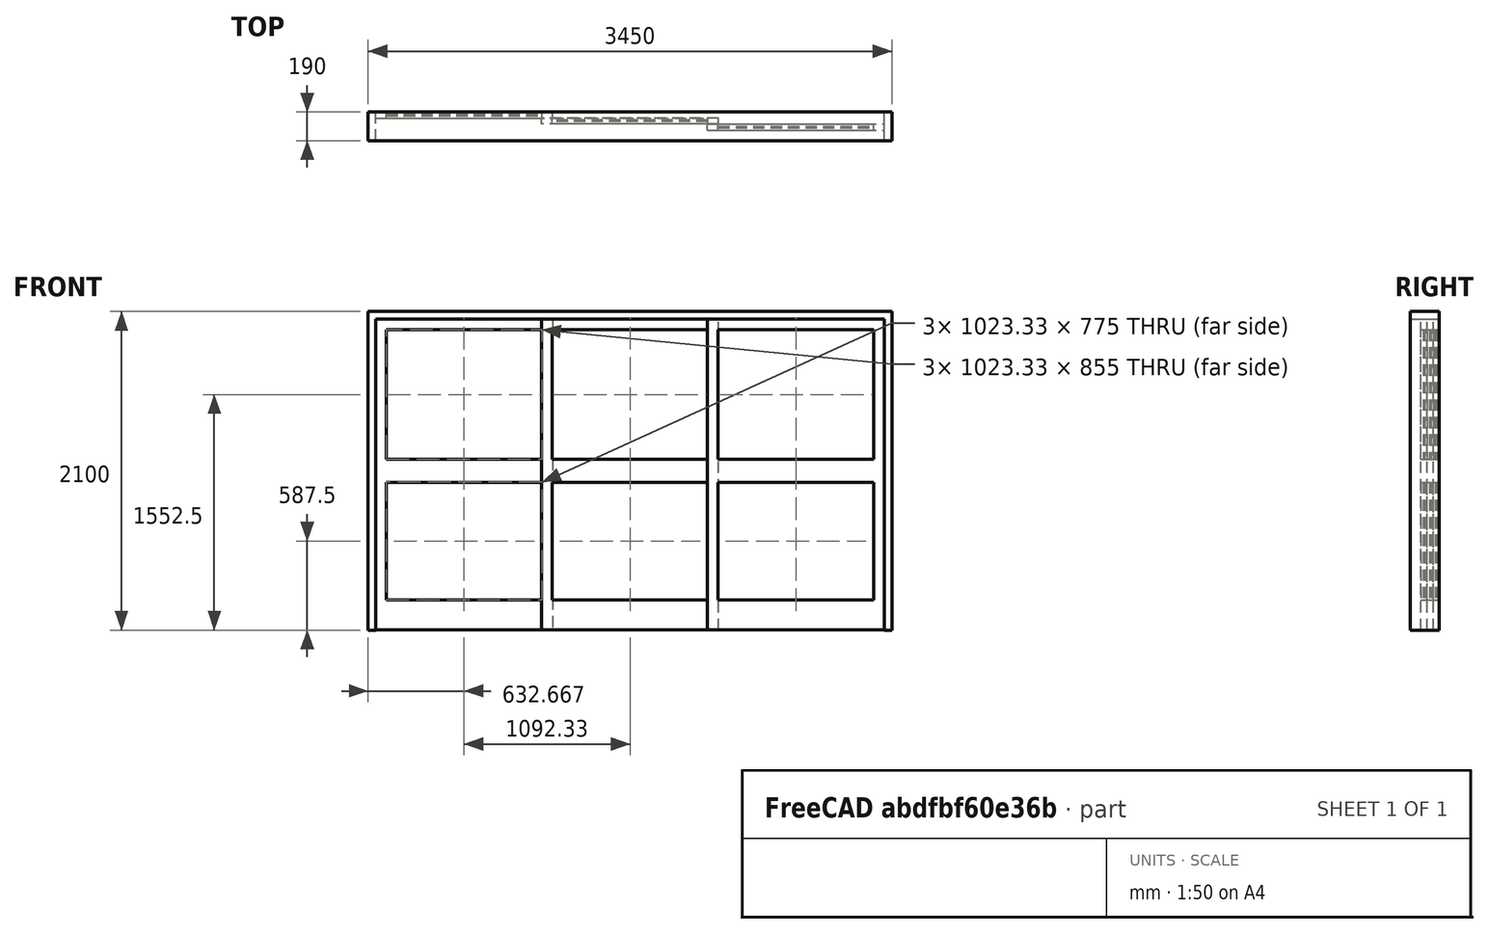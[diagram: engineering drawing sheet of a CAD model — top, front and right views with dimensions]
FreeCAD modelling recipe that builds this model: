
FCSTD DOCUMENT  (FreeCAD 0.16R6704 (Git))
Label: Slinding door 3 sheets with glass
License: CreativeCommons Attribution
LicenseURL: http://creativecommons.org/licenses/by/4.0/
objects: Sketcher::SketchObject×1, Part::FeaturePython×1
note: 2 computed .brp shape members not serialized (recipe doc carries the construction recipe); baked Part::Feature solids carry a one-line shape summary decoded from their .brp

FEATURE [Sketcher::SketchObject] Sketch182  label="Sketch"
  Placement = pos=(0,0,0) rot=(1,0,0;1.5708rad)
  sketch-geometry (45):
    g0: LineSegment StartX=0 StartY=0 StartZ=0 EndX=3450 EndY=0 EndZ=0
    g1: LineSegment StartX=3450 StartY=0 StartZ=0 EndX=3450 EndY=2100 EndZ=0
    g2: LineSegment StartX=3450 StartY=2100 StartZ=0 EndX=0 EndY=2100 EndZ=0
    g3: LineSegment StartX=0 StartY=2100 StartZ=0 EndX=0 EndY=0 EndZ=0
    g4: LineSegment StartX=50 StartY=0 StartZ=0 EndX=3400 EndY=0 EndZ=0
    g5: LineSegment StartX=3400 StartY=0 StartZ=0 EndX=3400 EndY=2050 EndZ=0
    g6: LineSegment StartX=3400 StartY=2050 StartZ=0 EndX=50 EndY=2050 EndZ=0
    g7: LineSegment StartX=50 StartY=2050 StartZ=0 EndX=50 EndY=0 EndZ=0
    g8: LineSegment StartX=121 StartY=1980 StartZ=0 EndX=1144.33 EndY=1980 EndZ=0
    g9: LineSegment StartX=1144.33 StartY=1980 StartZ=0 EndX=1144.33 EndY=1125 EndZ=0
    g10: LineSegment StartX=1144.33 StartY=1125 StartZ=0 EndX=121 EndY=1125 EndZ=0
    g11: LineSegment StartX=121 StartY=1125 StartZ=0 EndX=121 EndY=1980 EndZ=0
    g12: LineSegment StartX=121 StartY=975 StartZ=0 EndX=1144.33 EndY=975 EndZ=0
    g13: LineSegment StartX=1144.33 StartY=975 StartZ=0 EndX=1144.33 EndY=200 EndZ=0
    g14: LineSegment StartX=1144.33 StartY=200 StartZ=0 EndX=121 EndY=200 EndZ=0
    g15: LineSegment StartX=121 StartY=200 StartZ=0 EndX=121 EndY=975 EndZ=0
    g16: LineSegment [constr] StartX=-278 StartY=1050 StartZ=0 EndX=3676 EndY=1050 EndZ=0
    g17: LineSegment StartX=51 StartY=2049 StartZ=0 EndX=1214.33 EndY=2049 EndZ=0
    g18: LineSegment StartX=1214.33 StartY=2049 StartZ=0 EndX=1214.33 EndY=1 EndZ=0
    g19: LineSegment StartX=1214.33 StartY=1 StartZ=0 EndX=51 EndY=1 EndZ=0
    g20: LineSegment StartX=51 StartY=1 StartZ=0 EndX=51 EndY=2049 EndZ=0
    g21: LineSegment StartX=2236.67 StartY=1980 StartZ=0 EndX=1213.33 EndY=1980 EndZ=0
    g22: LineSegment StartX=1213.33 StartY=1980 StartZ=0 EndX=1213.33 EndY=1125 EndZ=0
    g23: LineSegment StartX=1213.33 StartY=1125 StartZ=0 EndX=2236.67 EndY=1125 EndZ=0
    g24: LineSegment StartX=2236.67 StartY=1125 StartZ=0 EndX=2236.67 EndY=1980 EndZ=0
    g25: LineSegment StartX=2236.67 StartY=975 StartZ=0 EndX=1213.33 EndY=975 EndZ=0
    g26: LineSegment StartX=1213.33 StartY=975 StartZ=0 EndX=1213.33 EndY=200 EndZ=0
    g27: LineSegment StartX=1213.33 StartY=200 StartZ=0 EndX=2236.67 EndY=200 EndZ=0
    g28: LineSegment StartX=2236.67 StartY=200 StartZ=0 EndX=2236.67 EndY=975 EndZ=0
    g29: LineSegment StartX=2306.67 StartY=2049 StartZ=0 EndX=1143.33 EndY=2049 EndZ=0
    g30: LineSegment StartX=1143.33 StartY=2049 StartZ=0 EndX=1143.33 EndY=1 EndZ=0
    g31: LineSegment StartX=1143.33 StartY=1 StartZ=0 EndX=2306.67 EndY=1 EndZ=0
    g32: LineSegment StartX=2306.67 StartY=1 StartZ=0 EndX=2306.67 EndY=2049 EndZ=0
    g33: LineSegment StartX=2305.67 StartY=1980 StartZ=0 EndX=3329 EndY=1980 EndZ=0
    g34: LineSegment StartX=3329 StartY=1980 StartZ=0 EndX=3329 EndY=1125 EndZ=0
    g35: LineSegment StartX=3329 StartY=1125 StartZ=0 EndX=2305.67 EndY=1125 EndZ=0
    g36: LineSegment StartX=2305.67 StartY=1125 StartZ=0 EndX=2305.67 EndY=1980 EndZ=0
    g37: LineSegment StartX=2305.67 StartY=975 StartZ=0 EndX=3329 EndY=975 EndZ=0
    g38: LineSegment StartX=3329 StartY=975 StartZ=0 EndX=3329 EndY=200 EndZ=0
    g39: LineSegment StartX=3329 StartY=200 StartZ=0 EndX=2305.67 EndY=200 EndZ=0
    g40: LineSegment StartX=2305.67 StartY=200 StartZ=0 EndX=2305.67 EndY=975 EndZ=0
    g41: LineSegment StartX=2235.67 StartY=2049 StartZ=0 EndX=3399 EndY=2049 EndZ=0
    g42: LineSegment StartX=3399 StartY=2049 StartZ=0 EndX=3399 EndY=1 EndZ=0
    g43: LineSegment StartX=3399 StartY=1 StartZ=0 EndX=2235.67 EndY=1 EndZ=0
    g44: LineSegment StartX=2235.67 StartY=1 StartZ=0 EndX=2235.67 EndY=2049 EndZ=0
  constraints (132):
    c: Coincident(g0,g1)
    c: Coincident(g1,g2)
    c: Coincident(g2,g3)
    c: Coincident(g3,g0)
    c: Horizontal(g0)
    c: Horizontal(g2)
    c: Vertical(g1)
    c: Vertical(g3)
    c: Coincident(g4,g5)
    c: Coincident(g5,g6)
    c: Coincident(g6,g7)
    c: Coincident(g7,g4)
    c: Horizontal(g4)
    c: Horizontal(g6)
    c: Vertical(g5)
    c: Vertical(g7)
    c: DistanceY(g1) = 2100  'Altura do vão'
    c: DistanceX(g0) = 3450  'Largura do vão'
    c: DistanceY(g6,g2) = 50  'Batente horizontal'
    c: DistanceX(g2,g6) = 50  'batente vertical 1'
    c: DistanceX(g4,g0) = 50  'Batente vertical 2'
    c: DistanceY(g0,g4) = 0
    c: Coincident(g0,g-1)
    c: Coincident(g8,g9)
    c: Coincident(g9,g10)
    c: Coincident(g10,g11)
    c: Coincident(g11,g8)
    c: Horizontal(g8)
    c: Horizontal(g10)
    c: Vertical(g9)
    c: Vertical(g11)
    c: Coincident(g12,g13)
    c: Coincident(g13,g14)
    c: Coincident(g14,g15)
    c: Coincident(g15,g12)
    c: Horizontal(g12)
    c: Horizontal(g14)
    c: Vertical(g13)
    c: Vertical(g15)
    c: DistanceX(g10,g12) = 0
    c: DistanceX(g9,g12) = 0
    c: DistanceY(g12,g10) = 150  'Montante intermediário portas'
    c: DistanceY(g8,g6) = 70  'Altura montante horizontal superior portas'
    c: DistanceY(g-1,g14) = 200  'Montante inferior portas'
    c: Horizontal(g16)
    c: Symmetric(g10,g12,g16)
    c: DistanceY(g-1,g16) = 1050  'Altura montante intermediário portas ao chão (eixo)'
    c: Coincident(g17,g18)
    c: Coincident(g18,g19)
    c: Coincident(g19,g20)
    c: Horizontal(g17)
    c: Horizontal(g19)
    c: Vertical(g18)
    c: Vertical(g20)
    c: DistanceY(g4,g18) = 1
    c: DistanceX(g6,g17) = 1
    c: DistanceY(g17,g6) = 1  'Constraint59'
    c: DistanceX(g8,g17) = 70  'Largura montante vertical 2 porta 1'
    c: DistanceX(g17,g8) = 70  'Largura montante porta 2'
    c: Coincident(g21,g22)
    c: Coincident(g22,g23)
    c: Coincident(g23,g24)
    c: Coincident(g24,g21)
    c: Horizontal(g21)
    c: Horizontal(g23)
    c: Vertical(g22)
    c: Vertical(g24)
    c: Coincident(g25,g26)
    c: Coincident(g26,g27)
    c: Coincident(g27,g28)
    c: Coincident(g28,g25)
    c: Horizontal(g25)
    c: Horizontal(g27)
    c: Vertical(g26)
    c: Vertical(g28)
    c: Coincident(g29,g30)
    c: Coincident(g30,g31)
    c: Coincident(g31,g32)
    c: Horizontal(g29)
    c: Horizontal(g31)
    c: Vertical(g30)
    c: Vertical(g32)
    c: DistanceY(g29,g5) = 1
    c: DistanceY(g8,g21) = 0
    c: DistanceY(g9,g22) = 0
    c: DistanceY(g25,g12) = 0
    c: DistanceY(g18,g30) = 0
    c: DistanceX(g23,g25) = 0
    c: Coincident(g29,g32)
    c: DistanceX(g29,g21) = 70  'Largura montante vertical 1 porta 2'
    c: DistanceX(g21,g29) = 70  'Largura montante vertical 2 porta 2'
    c: DistanceX(g22,g25) = 0  'Constraint95'
    c: DistanceX(g29,g8) = 1  'Constraint93'
    c: DistanceY(g26,g13) = 0
    c: Coincident(g33,g34)
    c: Coincident(g34,g35)
    c: Coincident(g35,g36)
    c: Coincident(g36,g33)
    c: Horizontal(g33)
    c: Horizontal(g35)
    c: Vertical(g34)
    c: Vertical(g36)
    c: Coincident(g37,g38)
    c: Coincident(g38,g39)
    c: Coincident(g39,g40)
    c: Coincident(g40,g37)
    c: Horizontal(g37)
    c: Horizontal(g39)
    c: Vertical(g38)
    c: Vertical(g40)
    c: Coincident(g41,g42)
    c: Coincident(g42,g43)
    c: Coincident(g43,g44)
    c: Horizontal(g41)
    c: Horizontal(g43)
    c: Vertical(g42)
    c: Vertical(g44)
    c: Coincident(g41,g44)
    c: DistanceY(g21,g33) = 0
    c: DistanceY(g23,g35) = 0
    c: DistanceY(g25,g37) = 0
    c: DistanceY(g31,g43) = 0
    c: DistanceX(g41,g33) = 70  'Montante vertical 1 porta 3'
    c: DistanceX(g33,g41) = 70  'Montante vertical 2 porta 3'
    c: DistanceX(g35,g37) = 0
    c: DistanceX(g34,g37) = 0
    c: DistanceX(g41,g21) = 1
    c: DistanceX(g41,g5) = 1
    c: Equal(g8,g21)
    c: Equal(g21,g33)
    c: DistanceY(g41,g29) = 0
    c: Coincident(g20,g17)
FEATURE [Part::FeaturePython] Window115  label="Slinding door 3 sheets with glass"  # WARN: FeaturePython — macro-defined, semantics opaque (R4)
  Base = -> Sketch182
  Height = 2100
  HoleDepth = 0
  MoveWithHost = true
  Normal = (0,1,0)
  Preset = 6
  Role = 1
  Width = 900
  WindowParts = BATENTE | Frame | Wire0,Wire1 | 190.0 | 0.0 | PORTA 1 | Frame | Wire2,Wire3,Wire4 | 40.0 | 150.0 | PORTA 2 | Frame | Wire5,Wire6,Wire7 | 40.0 | 110.0 | VIDRO SUPERIOR 1 | Glass panel | Wire2 | 10.0 | 165.0 | VIDRO SUPERIOR 2 | Glass panel | Wire5 | 10.0 | 125.0 | VIDRO INFERIOR 1 | Glass panel | Wire3 | 10.0 | 165.0 | VIDRO INFERIOR 2 | Glass panel | Wire6 | 10.0 | 125.0 | PORTA 3 | Frame | Wire10,Wire9,Wire8 | 40.0 | 70.0 | VIDRO SUPERIOR PORTA 3 | Glass panel | Wire8 | 10.0 | 85.0 | VIDRO INFERIOR PORTA 3 | Glass panel | Wire9 | 10.0 | 85.0
